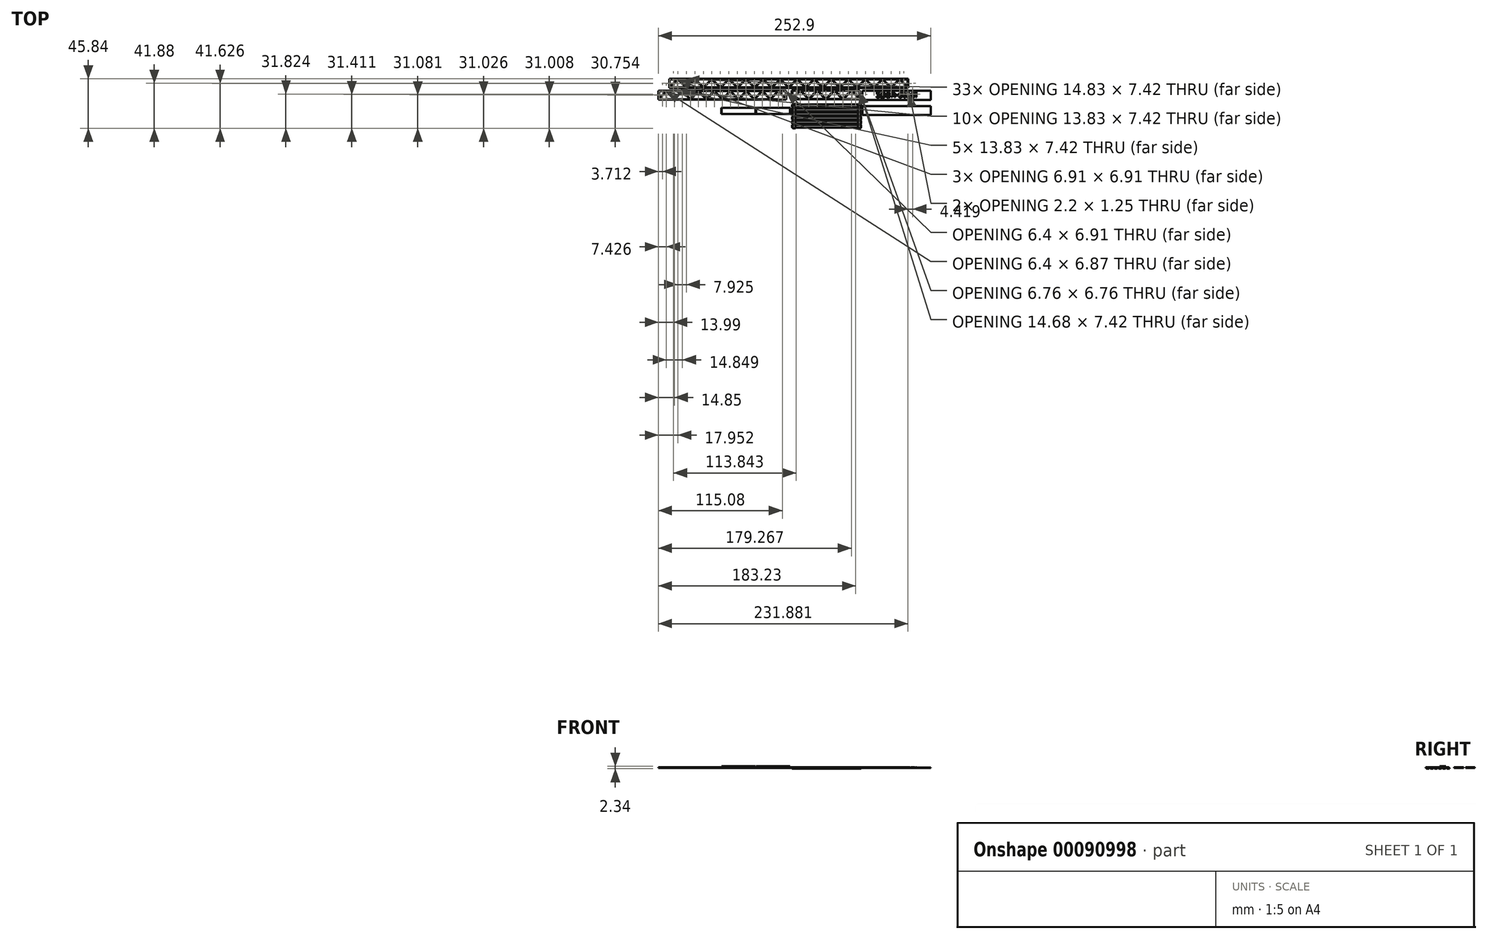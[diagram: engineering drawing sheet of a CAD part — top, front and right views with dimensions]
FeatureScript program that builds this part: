
annotation { "Feature Type Name" : "Feature", "Feature Type Description" : "" }
export const myFeature = defineFeature(function(context is Context, id is Id, definition is map)
    precondition{}
    {
        {
            var Q0;
            Q0=qCreatedBy(makeId("Top.planeOp"),FACE);
            var sketch = newSketch(context, id + "F0", { "sketchPlane" : qUnion([Q0])});
            skLineSegment(sketch, "E0.bottom", {"start": v(-2.9, 0) * mm, "end": v(-113.84, 0) * mm});
            skLineSegment(sketch, "E0.top", {"start": v(-2.9, 8.43) * mm, "end": v(-113.84, 8.43) * mm});
            skLineSegment(sketch, "E0.right", {"start": v(-113.84, 0) * mm, "end": v(-113.84, 8.43) * mm});
            skLineSegment(sketch, "E1.bottom", {"start": v(-113.33, 7.92) * mm, "end": v(-106.43, 7.92) * mm});
            skLineSegment(sketch, "E1.top", {"start": v(-113.33, 0.5) * mm, "end": v(-98.5, 0.5) * mm});
            skLineSegment(sketch, "E1.left", {"start": v(-113.33, 7.92) * mm, "end": v(-113.33, 1.02) * mm});
            skLineSegment(sketch, "E2", {"start": v(-113.33, 0.5) * mm, "end": v(-105.92, 7.92) * mm});
            skLineSegment(sketch, "E3", {"start": v(-113.33, 1.02) * mm, "end": v(-106.43, 7.92) * mm});
            skLineSegment(sketch, "E4.MirrorCS", {"start": v(-98.5, 0.5) * mm, "end": v(-105.92, 7.92) * mm});
            skLineSegment(sketch, "E5", {"start": v(-98, 0.5) * mm, "end": v(-105.41, 7.92) * mm});
            skLineSegment(sketch, "E6.MirrorCS", {"start": v(-98, 0.5) * mm, "end": v(-90.58, 7.92) * mm});
            skLineSegment(sketch, "E7.MirrorCS", {"start": v(-97.49, 0.5) * mm, "end": v(-90.07, 7.92) * mm});
            skLineSegment(sketch, "E8.MirrorCS", {"start": v(-82.65, 0.5) * mm, "end": v(-90.07, 7.92) * mm});
            skLineSegment(sketch, "E9.MirrorCS", {"start": v(-82.14, 0.5) * mm, "end": v(-89.56, 7.92) * mm});
            skLineSegment(sketch, "E10.MirrorCS", {"start": v(-82.14, 0.5) * mm, "end": v(-74.73, 7.92) * mm});
            skLineSegment(sketch, "E11.MirrorCS", {"start": v(-81.64, 0.5) * mm, "end": v(-74.22, 7.92) * mm});
            skLineSegment(sketch, "E12.MirrorCS", {"start": v(-66.8, 0.5) * mm, "end": v(-74.22, 7.92) * mm});
            skLineSegment(sketch, "E13.MirrorCS", {"start": v(-66.3, 0.5) * mm, "end": v(-73.71, 7.92) * mm});
            skLineSegment(sketch, "E14.MirrorCS", {"start": v(-66.3, 0.5) * mm, "end": v(-58.88, 7.92) * mm});
            skLineSegment(sketch, "E15.MirrorCS", {"start": v(-65.79, 0.5) * mm, "end": v(-58.37, 7.92) * mm});
            skLineSegment(sketch, "E16.MirrorCS", {"start": v(-50.95, 0.5) * mm, "end": v(-58.37, 7.92) * mm});
            skLineSegment(sketch, "E17.MirrorCS", {"start": v(-50.44, 0.5) * mm, "end": v(-57.86, 7.92) * mm});
            skLineSegment(sketch, "E18.MirrorCS", {"start": v(-50.44, 0.5) * mm, "end": v(-43.03, 7.92) * mm});
            skLineSegment(sketch, "E19.MirrorCS", {"start": v(-49.94, 0.5) * mm, "end": v(-42.52, 7.92) * mm});
            skLineSegment(sketch, "E20.MirrorCS", {"start": v(-35.1, 0.5) * mm, "end": v(-42.52, 7.92) * mm});
            skLineSegment(sketch, "E21.MirrorCS", {"start": v(-34.6, 0.5) * mm, "end": v(-42.01, 7.92) * mm});
            skLineSegment(sketch, "E22.MirrorCS", {"start": v(-34.6, 0.5) * mm, "end": v(-27.18, 7.92) * mm});
            skLineSegment(sketch, "E23.MirrorCS", {"start": v(-34.09, 0.5) * mm, "end": v(-26.67, 7.92) * mm});
            skLineSegment(sketch, "E24.MirrorCS", {"start": v(-19.25, 0.5) * mm, "end": v(-26.67, 7.92) * mm});
            skLineSegment(sketch, "E25.MirrorCS", {"start": v(-18.75, 0.5) * mm, "end": v(-26.16, 7.92) * mm});
            skLineSegment(sketch, "E26.MirrorCS", {"start": v(-18.75, 0.5) * mm, "end": v(-11.33, 7.92) * mm});
            skLineSegment(sketch, "E27.MirrorCS", {"start": v(-18.24, 0.5) * mm, "end": v(-10.82, 7.92) * mm});
            skLineSegment(sketch, "E28.MirrorCS", {"start": v(-2.9, 0.5) * mm, "end": v(-10.31, 7.92) * mm});
            skLineSegment(sketch, "E29.MirrorCS", {"start": v(-3.4, 0.5) * mm, "end": v(-10.82, 7.92) * mm});
            skLineSegment(sketch, "E30", {"start": v(-2.9, 0.5) * mm, "end": v(-2.9, 7.92) * mm});
            skLineSegment(sketch, "E31", {"start": v(-2.9, 7.92) * mm, "end": v(-2.9, 8.43) * mm});
            skLineSegment(sketch, "E32", {"start": v(-2.9, 8.43) * mm, "end": v(-2.9, 7.92) * mm});
            skLineSegment(sketch, "E33.trimOffspring", {"start": v(-10.31, 7.92) * mm, "end": v(-2.9, 7.92) * mm});
            skLineSegment(sketch, "E34.trimOffspring", {"start": v(-18.24, 0.5) * mm, "end": v(-3.4, 0.5) * mm});
            skLineSegment(sketch, "E35.trimOffspring", {"start": v(-26.16, 7.92) * mm, "end": v(-11.33, 7.92) * mm});
            skLineSegment(sketch, "E36.trimOffspring", {"start": v(-34.09, 0.5) * mm, "end": v(-19.25, 0.5) * mm});
            skLineSegment(sketch, "E37.trimOffspring", {"start": v(-49.94, 0.5) * mm, "end": v(-35.1, 0.5) * mm});
            skLineSegment(sketch, "E38.trimOffspring", {"start": v(-42.01, 7.92) * mm, "end": v(-27.18, 7.92) * mm});
            skLineSegment(sketch, "E39.trimOffspring", {"start": v(-57.86, 7.92) * mm, "end": v(-43.03, 7.92) * mm});
            skLineSegment(sketch, "E40.trimOffspring", {"start": v(-65.79, 0.5) * mm, "end": v(-50.95, 0.5) * mm});
            skLineSegment(sketch, "E41.trimOffspring", {"start": v(-81.64, 0.5) * mm, "end": v(-66.8, 0.5) * mm});
            skLineSegment(sketch, "E42.trimOffspring", {"start": v(-97.49, 0.5) * mm, "end": v(-82.65, 0.5) * mm});
            skLineSegment(sketch, "E43.trimOffspring", {"start": v(-105.41, 7.92) * mm, "end": v(-90.58, 7.92) * mm});
            skLineSegment(sketch, "E44.trimOffspring", {"start": v(-89.56, 7.92) * mm, "end": v(-74.73, 7.92) * mm});
            skLineSegment(sketch, "E45.trimOffspring", {"start": v(-73.71, 7.92) * mm, "end": v(-58.88, 7.92) * mm});
            skLineSegment(sketch, "E46.MirrorCS", {"start": v(12.95, 0.5) * mm, "end": v(20.37, 7.92) * mm});
            skLineSegment(sketch, "E47.MirrorCS", {"start": v(36.22, 7.92) * mm, "end": v(21.39, 7.92) * mm});
            skLineSegment(sketch, "E48.MirrorCS", {"start": v(28.8, 0.5) * mm, "end": v(21.39, 7.92) * mm});
            skLineSegment(sketch, "E49.MirrorCS", {"start": v(12.45, 0.5) * mm, "end": v(-2.39, 0.5) * mm});
            skLineSegment(sketch, "E50.MirrorCS", {"start": v(28.3, 0.5) * mm, "end": v(20.88, 7.92) * mm});
            skLineSegment(sketch, "E51.MirrorCS", {"start": v(-2.9, 8.43) * mm, "end": v(108.05, 8.43) * mm});
            skLineSegment(sketch, "E52.MirrorCS", {"start": v(12.95, 0.5) * mm, "end": v(5.54, 7.92) * mm});
            skLineSegment(sketch, "E53.MirrorCS", {"start": v(44.15, 0.5) * mm, "end": v(29.31, 0.5) * mm});
            skLineSegment(sketch, "E54.MirrorCS", {"start": v(28.3, 0.5) * mm, "end": v(13.46, 0.5) * mm});
            skLineSegment(sketch, "E55.MirrorCS", {"start": v(4.52, 7.92) * mm, "end": v(-2.9, 7.92) * mm});
            skLineSegment(sketch, "E56.MirrorCS", {"start": v(28.8, 0.5) * mm, "end": v(36.22, 7.92) * mm});
            skLineSegment(sketch, "E57.MirrorCS", {"start": v(13.46, 0.5) * mm, "end": v(20.88, 7.92) * mm});
            skLineSegment(sketch, "E58.MirrorCS", {"start": v(12.45, 0.5) * mm, "end": v(5.03, 7.92) * mm});
            skLineSegment(sketch, "E59.MirrorCS", {"start": v(29.31, 0.5) * mm, "end": v(36.73, 7.92) * mm});
            skLineSegment(sketch, "E60.MirrorCS", {"start": v(-2.9, 0.5) * mm, "end": v(4.52, 7.92) * mm});
            skLineSegment(sketch, "E61.MirrorCS", {"start": v(20.37, 7.92) * mm, "end": v(5.54, 7.92) * mm});
            skLineSegment(sketch, "E62.MirrorCS", {"start": v(-2.39, 0.5) * mm, "end": v(5.03, 7.92) * mm});
            skLineSegment(sketch, "E63.MirrorCS", {"start": v(-2.9, 0) * mm, "end": v(108.05, 0) * mm});
            skLineSegment(sketch, "E64.MirrorCS", {"start": v(107.54, 0.5) * mm, "end": v(100.13, 7.92) * mm});
            skLineSegment(sketch, "E65.MirrorCS", {"start": v(83.77, 7.92) * mm, "end": v(68.94, 7.92) * mm});
            skLineSegment(sketch, "E66.MirrorCS", {"start": v(61.01, 0.5) * mm, "end": v(68.43, 7.92) * mm});
            skLineSegment(sketch, "E67.MirrorCS", {"start": v(44.15, 0.5) * mm, "end": v(36.73, 7.92) * mm});
            skLineSegment(sketch, "E68.MirrorCS", {"start": v(99.62, 7.92) * mm, "end": v(84.79, 7.92) * mm});
            skLineSegment(sketch, "E69.MirrorCS", {"start": v(75.84, 0.5) * mm, "end": v(68.43, 7.92) * mm});
            skLineSegment(sketch, "E70.MirrorCS", {"start": v(44.65, 0.5) * mm, "end": v(37.24, 7.92) * mm});
            skLineSegment(sketch, "E71.MirrorCS", {"start": v(91.7, 0.5) * mm, "end": v(76.86, 0.5) * mm});
            skLineSegment(sketch, "E72.MirrorCS", {"start": v(76.35, 0.5) * mm, "end": v(68.94, 7.92) * mm});
            skLineSegment(sketch, "E73.MirrorCS", {"start": v(92.2, 0.5) * mm, "end": v(84.79, 7.92) * mm});
            skLineSegment(sketch, "E74.MirrorCS", {"start": v(108.05, 0) * mm, "end": v(108.05, 8.43) * mm});
            skLineSegment(sketch, "E75.MirrorCS", {"start": v(107.54, 7.92) * mm, "end": v(107.54, 1.02) * mm});
            skLineSegment(sketch, "E76.MirrorCS", {"start": v(107.54, 1.02) * mm, "end": v(100.63, 7.92) * mm});
            skLineSegment(sketch, "E77.MirrorCS", {"start": v(107.54, 7.92) * mm, "end": v(100.63, 7.92) * mm});
            skLineSegment(sketch, "E78.MirrorCS", {"start": v(76.35, 0.5) * mm, "end": v(83.77, 7.92) * mm});
            skLineSegment(sketch, "E79.MirrorCS", {"start": v(76.86, 0.5) * mm, "end": v(84.28, 7.92) * mm});
            skLineSegment(sketch, "E80.MirrorCS", {"start": v(107.54, 0.5) * mm, "end": v(92.7, 0.5) * mm});
            skLineSegment(sketch, "E81.MirrorCS", {"start": v(60.5, 0.5) * mm, "end": v(53.09, 7.92) * mm});
            skLineSegment(sketch, "E82.MirrorCS", {"start": v(52.07, 7.92) * mm, "end": v(37.24, 7.92) * mm});
            skLineSegment(sketch, "E83.MirrorCS", {"start": v(91.7, 0.5) * mm, "end": v(84.28, 7.92) * mm});
            skLineSegment(sketch, "E84.MirrorCS", {"start": v(67.92, 7.92) * mm, "end": v(53.09, 7.92) * mm});
            skLineSegment(sketch, "E85.MirrorCS", {"start": v(60, 0.5) * mm, "end": v(52.58, 7.92) * mm});
            skLineSegment(sketch, "E86.MirrorCS", {"start": v(75.84, 0.5) * mm, "end": v(61.01, 0.5) * mm});
            skLineSegment(sketch, "E87.MirrorCS", {"start": v(45.16, 0.5) * mm, "end": v(52.58, 7.92) * mm});
            skLineSegment(sketch, "E88.MirrorCS", {"start": v(60, 0.5) * mm, "end": v(45.16, 0.5) * mm});
            skLineSegment(sketch, "E89.MirrorCS", {"start": v(60.5, 0.5) * mm, "end": v(67.92, 7.92) * mm});
            skLineSegment(sketch, "E90.MirrorCS", {"start": v(44.65, 0.5) * mm, "end": v(52.07, 7.92) * mm});
            skLineSegment(sketch, "E91.MirrorCS", {"start": v(92.7, 0.5) * mm, "end": v(100.13, 7.92) * mm});
            skLineSegment(sketch, "E92.MirrorCS", {"start": v(92.2, 0.5) * mm, "end": v(99.62, 7.92) * mm});
            skPoint(sketch, "E93.MirrorCS.end.orphan", {"position": v(-2.9, 8.43) * mm});
            skPoint(sketch, "E94.MirrorCS.end.orphan", {"position": v(103.58, 4.47) * mm});
            skPoint(sketch, "E94.MirrorCS.start.orphan", {"position": v(104.09, 4.47) * mm});
            skPoint(sketch, "E95.MirrorCS.end.orphan", {"position": v(107.04, 1.02) * mm});
            skPoint(sketch, "E96.end.orphan", {"position": v(-109.37, 4.47) * mm});
            skPoint(sketch, "E96.start.orphan", {"position": v(-109.88, 4.47) * mm});
            skPoint(sketch, "E97.end.orphan", {"position": v(-112.83, 1.02) * mm});
            skSolve(sketch);
        }
        {
            var Q0;
            Q0 = qSketchRegion(id + "F0", true);
            extrude(context, id + "F1", {"entities" : qUnion([Q0]), "depth" : 0.5 * mm});
        }
        {
            var Q0;
            Q0=qCreatedBy(makeId("Top.planeOp"),FACE);
            var sketch = newSketch(context, id + "F2", { "sketchPlane" : qUnion([Q0])});
            skLineSegment(sketch, "E98.bottom", {"start": v(0, -2.11) * mm, "end": v(63.25, -2.11) * mm});
            skLineSegment(sketch, "E98.top", {"start": v(0, -10.55) * mm, "end": v(63.25, -10.55) * mm});
            skLineSegment(sketch, "E98.left", {"start": v(0, -2.11) * mm, "end": v(0, -10.55) * mm});
            skLineSegment(sketch, "E98.right", {"start": v(63.25, -2.11) * mm, "end": v(63.25, -10.55) * mm});
            skLineSegment(sketch, "E99.bottom", {"start": v(0.5, -2.62) * mm, "end": v(7.42, -2.62) * mm});
            skLineSegment(sketch, "E99.top", {"start": v(0.5, -10.04) * mm, "end": v(15.34, -10.04) * mm});
            skLineSegment(sketch, "E99.left", {"start": v(0.5, -2.62) * mm, "end": v(0.5, -9.53) * mm});
            skLineSegment(sketch, "E99.right", {"start": v(62.74, -2.62) * mm, "end": v(62.74, -9.38) * mm});
            skLineSegment(sketch, "E100", {"start": v(0.5, -10.04) * mm, "end": v(7.92, -2.62) * mm});
            skLineSegment(sketch, "E101", {"start": v(0.5, -9.53) * mm, "end": v(7.42, -2.62) * mm});
            skLineSegment(sketch, "E102.MirrorCS", {"start": v(15.34, -10.04) * mm, "end": v(7.92, -2.62) * mm});
            skLineSegment(sketch, "E103", {"start": v(15.85, -10.04) * mm, "end": v(8.43, -2.62) * mm});
            skLineSegment(sketch, "E104.trimOffspring", {"start": v(16.36, -10.04) * mm, "end": v(47.04, -10.04) * mm});
            skLineSegment(sketch, "E105.trimOffspring", {"start": v(8.43, -2.62) * mm, "end": v(23.27, -2.62) * mm});
            skLineSegment(sketch, "E106.MirrorCS", {"start": v(15.85, -10.04) * mm, "end": v(23.27, -2.62) * mm});
            skLineSegment(sketch, "E107.MirrorCS", {"start": v(16.36, -10.04) * mm, "end": v(23.77, -2.62) * mm});
            skLineSegment(sketch, "E108.trimOffspring", {"start": v(24.28, -2.62) * mm, "end": v(39.12, -2.62) * mm});
            skLineSegment(sketch, "E109.MirrorCS", {"start": v(31.2, -10.04) * mm, "end": v(23.77, -2.62) * mm});
            skLineSegment(sketch, "E110.MirrorCS", {"start": v(31.7, -10.04) * mm, "end": v(24.28, -2.62) * mm});
            skLineSegment(sketch, "E111.MirrorCS", {"start": v(31.7, -10.04) * mm, "end": v(39.12, -2.62) * mm});
            skLineSegment(sketch, "E112.MirrorCS", {"start": v(32.2, -10.04) * mm, "end": v(39.62, -2.62) * mm});
            skLineSegment(sketch, "E113.trimOffspring", {"start": v(40.13, -2.62) * mm, "end": v(54.97, -2.62) * mm});
            skLineSegment(sketch, "E114.MirrorCS", {"start": v(47.55, -10.04) * mm, "end": v(40.13, -2.62) * mm});
            skLineSegment(sketch, "E115.MirrorCS", {"start": v(47.04, -10.04) * mm, "end": v(39.62, -2.62) * mm});
            skLineSegment(sketch, "E116.MirrorCS", {"start": v(47.55, -10.04) * mm, "end": v(54.97, -2.62) * mm});
            skLineSegment(sketch, "E117.MirrorCS", {"start": v(48.06, -10.04) * mm, "end": v(55.47, -2.62) * mm});
            skLineSegment(sketch, "E118.trimOffspring", {"start": v(55.98, -2.62) * mm, "end": v(62.74, -2.62) * mm});
            skLineSegment(sketch, "E119.trimOffspring", {"start": v(62.74, -9.38) * mm, "end": v(55.98, -2.62) * mm});
            skLineSegment(sketch, "E120.trimOffspring", {"start": v(48.06, -10.04) * mm, "end": v(62.74, -10.04) * mm});
            skLineSegment(sketch, "E121", {"start": v(62.74, -10.04) * mm, "end": v(55.47, -2.62) * mm});
            skSolve(sketch);
        }
        {
            var Q0;
            Q0 = qSketchRegion(id + "F2", true);
            extrude(context, id + "F3", {"entities" : qUnion([Q0]), "depth" : 0.5 * mm});
        }
        {
            var Q0;
            Q0=qCreatedBy(makeId("Top.planeOp"),FACE);
            var sketch = newSketch(context, id + "F4", { "sketchPlane" : qUnion([Q0])});
            skLineSegment(sketch, "E122.bottom", {"start": v(-5.08, -2.44) * mm, "end": v(-123.36, -2.44) * mm});
            skLineSegment(sketch, "E122.top", {"start": v(-5.08, -10.87) * mm, "end": v(-123.36, -10.87) * mm});
            skLineSegment(sketch, "E122.left", {"start": v(-5.08, -2.44) * mm, "end": v(-5.08, -10.87) * mm});
            skLineSegment(sketch, "E123.bottom", {"start": v(-5.59, -2.95) * mm, "end": v(-12, -2.95) * mm});
            skLineSegment(sketch, "E123.top", {"start": v(-5.59, -10.36) * mm, "end": v(-19.42, -10.36) * mm});
            skLineSegment(sketch, "E123.left", {"start": v(-5.59, -2.95) * mm, "end": v(-5.59, -9.86) * mm});
            skLineSegment(sketch, "E124", {"start": v(-5.59, -10.36) * mm, "end": v(-12.5, -2.95) * mm});
            skLineSegment(sketch, "E125", {"start": v(-12, -2.95) * mm, "end": v(-5.59, -9.86) * mm});
            skLineSegment(sketch, "E126.MirrorCS", {"start": v(-19.42, -10.36) * mm, "end": v(-12.5, -2.95) * mm});
            skLineSegment(sketch, "E127.MirrorCS", {"start": v(-13.02, -2.95) * mm, "end": v(-19.37, -9.77) * mm});
            skLineSegment(sketch, "E128.trimOffspring", {"start": v(-13.02, -2.95) * mm, "end": v(-26.84, -2.95) * mm});
            skLineSegment(sketch, "E129", {"start": v(-19.37, -9.77) * mm, "end": v(-19.93, -10.36) * mm});
            skLineSegment(sketch, "E130.trimOffspring", {"start": v(-20.44, -10.36) * mm, "end": v(-34.27, -10.36) * mm});
            skLineSegment(sketch, "E131", {"start": v(-19.93, -10.36) * mm, "end": v(-13.02, -2.95) * mm});
            skLineSegment(sketch, "E132.MirrorCS", {"start": v(-19.93, -10.36) * mm, "end": v(-26.84, -2.95) * mm});
            skLineSegment(sketch, "E133.MirrorCS", {"start": v(-20.44, -10.36) * mm, "end": v(-27.35, -2.95) * mm});
            skLineSegment(sketch, "E134.trimOffspring", {"start": v(-27.86, -2.95) * mm, "end": v(-41.7, -2.95) * mm});
            skLineSegment(sketch, "E135.MirrorCS", {"start": v(-34.27, -10.36) * mm, "end": v(-27.35, -2.95) * mm});
            skLineSegment(sketch, "E136.MirrorCS", {"start": v(-34.78, -10.36) * mm, "end": v(-27.86, -2.95) * mm});
            skLineSegment(sketch, "E137.MirrorCS", {"start": v(-35.29, -10.36) * mm, "end": v(-42.2, -2.95) * mm});
            skLineSegment(sketch, "E138.MirrorCS", {"start": v(-41.7, -2.95) * mm, "end": v(-35.33, -9.77) * mm});
            skLineSegment(sketch, "E139.trimOffspring", {"start": v(-35.29, -10.36) * mm, "end": v(-49.12, -10.36) * mm});
            skLineSegment(sketch, "E140", {"start": v(-34.78, -10.36) * mm, "end": v(-35.33, -9.77) * mm});
            skLineSegment(sketch, "E141.trimOffspring", {"start": v(-42.71, -2.95) * mm, "end": v(-56.54, -2.95) * mm});
            skLineSegment(sketch, "E142.MirrorCS", {"start": v(-49.12, -10.36) * mm, "end": v(-42.2, -2.95) * mm});
            skLineSegment(sketch, "E143.MirrorCS", {"start": v(-42.71, -2.95) * mm, "end": v(-49.07, -9.77) * mm});
            skLineSegment(sketch, "E144.MirrorCS", {"start": v(-49.63, -10.36) * mm, "end": v(-49.07, -9.77) * mm});
            skLineSegment(sketch, "E145.MirrorCS", {"start": v(-49.63, -10.36) * mm, "end": v(-56.54, -2.95) * mm});
            skLineSegment(sketch, "E146.MirrorCS", {"start": v(-50.13, -10.36) * mm, "end": v(-57.05, -2.95) * mm});
            skLineSegment(sketch, "E147.MirrorCS", {"start": v(-64.47, -10.36) * mm, "end": v(-57.56, -2.95) * mm});
            skLineSegment(sketch, "E148.MirrorCS", {"start": v(-63.97, -10.36) * mm, "end": v(-57.05, -2.95) * mm});
            skLineSegment(sketch, "E149.MirrorCS", {"start": v(-71.39, -2.95) * mm, "end": v(-65.03, -9.77) * mm});
            skLineSegment(sketch, "E150.MirrorCS", {"start": v(-64.98, -10.36) * mm, "end": v(-71.9, -2.95) * mm});
            skLineSegment(sketch, "E151.MirrorCS", {"start": v(-64.47, -10.36) * mm, "end": v(-71.39, -2.95) * mm});
            skLineSegment(sketch, "E152.trimOffspring", {"start": v(-50.13, -10.36) * mm, "end": v(-63.97, -10.36) * mm});
            skLineSegment(sketch, "E153.trimOffspring", {"start": v(-64.98, -10.36) * mm, "end": v(-78.81, -10.36) * mm});
            skLineSegment(sketch, "E154.trimOffspring", {"start": v(-57.56, -2.95) * mm, "end": v(-71.39, -2.95) * mm});
            skLineSegment(sketch, "E155.trimOffspring", {"start": v(-72.4, -2.95) * mm, "end": v(-86.24, -2.95) * mm});
            skLineSegment(sketch, "E156.MirrorCS", {"start": v(-78.81, -10.36) * mm, "end": v(-71.9, -2.95) * mm});
            skLineSegment(sketch, "E157.MirrorCS", {"start": v(-72.4, -2.95) * mm, "end": v(-78.76, -9.77) * mm});
            skLineSegment(sketch, "E158.MirrorCS", {"start": v(-79.32, -10.36) * mm, "end": v(-86.24, -2.95) * mm});
            skLineSegment(sketch, "E159.MirrorCS", {"start": v(-79.83, -10.36) * mm, "end": v(-86.75, -2.95) * mm});
            skLineSegment(sketch, "E160.MirrorCS", {"start": v(-79.32, -10.36) * mm, "end": v(-72.4, -2.95) * mm});
            skLineSegment(sketch, "E161.MirrorCS", {"start": v(-93.66, -10.36) * mm, "end": v(-86.75, -2.95) * mm});
            skLineSegment(sketch, "E162.MirrorCS", {"start": v(-94.17, -10.36) * mm, "end": v(-87.26, -2.95) * mm});
            skLineSegment(sketch, "E163.MirrorCS", {"start": v(-94.17, -10.36) * mm, "end": v(-94.73, -9.77) * mm});
            skLineSegment(sketch, "E164.MirrorCS", {"start": v(-94.68, -10.36) * mm, "end": v(-101.6, -2.95) * mm});
            skLineSegment(sketch, "E165.MirrorCS", {"start": v(-108.51, -10.36) * mm, "end": v(-101.6, -2.95) * mm});
            skLineSegment(sketch, "E166.MirrorCS", {"start": v(-109.02, -10.36) * mm, "end": v(-108.46, -9.77) * mm});
            skLineSegment(sketch, "E167.MirrorCS", {"start": v(-102.1, -2.95) * mm, "end": v(-108.46, -9.77) * mm});
            skLineSegment(sketch, "E168.MirrorCS", {"start": v(-109.02, -10.36) * mm, "end": v(-115.93, -2.95) * mm});
            skLineSegment(sketch, "E169.MirrorCS", {"start": v(-109.53, -10.36) * mm, "end": v(-116.44, -2.95) * mm});
            skLineSegment(sketch, "E170.MirrorCS", {"start": v(-123.36, -10.36) * mm, "end": v(-116.44, -2.95) * mm});
            skLineSegment(sketch, "E171.MirrorCS", {"start": v(-123.36, -9.82) * mm, "end": v(-116.96, -2.95) * mm});
            skLineSegment(sketch, "E172.MirrorCS", {"start": v(-101.08, -2.95) * mm, "end": v(-94.73, -9.77) * mm});
            skLineSegment(sketch, "E173.trimOffspring", {"start": v(-79.83, -10.36) * mm, "end": v(-93.66, -10.36) * mm});
            skLineSegment(sketch, "E174.trimOffspring", {"start": v(-87.26, -2.95) * mm, "end": v(-101.08, -2.95) * mm});
            skLineSegment(sketch, "E175.trimOffspring", {"start": v(-94.68, -10.36) * mm, "end": v(-108.51, -10.36) * mm});
            skLineSegment(sketch, "E176.trimOffspring", {"start": v(-109.53, -10.36) * mm, "end": v(-123.36, -10.36) * mm});
            skLineSegment(sketch, "E177.trimOffspring", {"start": v(-102.1, -2.95) * mm, "end": v(-115.93, -2.95) * mm});
            skLineSegment(sketch, "E178.trimOffspring", {"start": v(-116.96, -2.95) * mm, "end": v(-123.36, -2.95) * mm});
            skLineSegment(sketch, "E179", {"start": v(-123.36, -9.82) * mm, "end": v(-123.36, -2.95) * mm});
            skLineSegment(sketch, "E180", {"start": v(-123.36, -2.95) * mm, "end": v(-123.36, -9.82) * mm});
            skLineSegment(sketch, "E181", {"start": v(-123.36, -10.87) * mm, "end": v(-123.87, -10.87) * mm});
            skLineSegment(sketch, "E182", {"start": v(-123.87, -10.87) * mm, "end": v(-123.87, -2.44) * mm});
            skLineSegment(sketch, "E183", {"start": v(-123.87, -2.44) * mm, "end": v(-123.36, -2.44) * mm});
            skSolve(sketch);
        }
        {
            var Q0;
            Q0 = qSketchRegion(id + "F4", true);
            extrude(context, id + "F5", {"entities" : qUnion([Q0]), "depth" : 0.5 * mm});
        }
        {
            var Q0;
            Q0=qCreatedBy(makeId("Top.planeOp"),FACE);
            var sketch = newSketch(context, id + "F6", { "sketchPlane" : qUnion([Q0])});
            skLineSegment(sketch, "E184.bottom", {"start": v(65.79, -2.54) * mm, "end": v(129.03, -2.54) * mm});
            skLineSegment(sketch, "E184.top", {"start": v(65.79, -10.97) * mm, "end": v(129.03, -10.97) * mm});
            skLineSegment(sketch, "E184.left", {"start": v(65.79, -2.54) * mm, "end": v(65.79, -10.97) * mm});
            skLineSegment(sketch, "E184.right", {"start": v(129.03, -2.54) * mm, "end": v(129.03, -10.97) * mm});
            skText(sketch, "E185", { "text": "Span-steel", "fontName": "OpenSans-Regular.ttf"});
            skLineSegment(sketch, "E186", {"start": v(83.43, -13.84) * mm, "end": v(94.5, -13.84) * mm});
            skLineSegment(sketch, "E187.MirrorCS", {"start": v(65.79, -16.7) * mm, "end": v(129.03, -16.7) * mm});
            skLineSegment(sketch, "E188.MirrorCS", {"start": v(65.79, -25.13) * mm, "end": v(65.79, -16.7) * mm});
            skLineSegment(sketch, "E189.MirrorCS", {"start": v(65.79, -25.13) * mm, "end": v(129.03, -25.13) * mm});
            skLineSegment(sketch, "E190.MirrorCS", {"start": v(129.03, -25.13) * mm, "end": v(129.03, -16.7) * mm});
            const initialGuessF6  = {"E185": [0.07836, -0.00872, 1, 0, 0.00567]};
            skSetInitialGuess(sketch, initialGuessF6);
            skSolve(sketch);
        }
        {
            var Q0;
            Q0 = qSketchRegion(id + "F6", true);
            var Q1;
            Q1=makeQuery(id+"F6.imprint","IMPRINT",FACE,{"disambiguationData":[TD([[makeQuery(id+"F6.imprint","IMPRINT",EDGE,{"derivedFrom":sQuery(id+"F6.wireOp",EDGE,"E185.sketch_text.stroke-50")}),-1.0]])]});
            var Q2;
            Q2=makeQuery(id+"F6.imprint","IMPRINT",FACE,{"disambiguationData":[TD([[makeQuery(id+"F6.imprint","IMPRINT",EDGE,{"derivedFrom":sQuery(id+"F6.wireOp",EDGE,"E185.sketch_text.stroke-0")}),-1.0]])]});
            var Q3;
            Q3=makeQuery(id+"F6.imprint","IMPRINT",FACE,{"disambiguationData":[TD([[makeQuery(id+"F6.imprint","IMPRINT",EDGE,{"derivedFrom":sQuery(id+"F6.wireOp",EDGE,"E185.sketch_text.stroke-41")}),1.0]])]});
            var Q4;
            Q4=makeQuery(id+"F6.imprint","IMPRINT",FACE,{"disambiguationData":[TD([[makeQuery(id+"F6.imprint","IMPRINT",EDGE,{"derivedFrom":sQuery(id+"F6.wireOp",EDGE,"E185.sketch_text.stroke-94")}),-1.0]])]});
            var Q5;
            Q5=makeQuery(id+"F6.imprint","IMPRINT",FACE,{"disambiguationData":[TD([[makeQuery(id+"F6.imprint","IMPRINT",EDGE,{"derivedFrom":sQuery(id+"F6.wireOp",EDGE,"E185.sketch_text.stroke-123")}),-1.0]])]});
            var Q6;
            Q6=makeQuery(id+"F6.imprint","IMPRINT",FACE,{"disambiguationData":[TD([[makeQuery(id+"F6.imprint","IMPRINT",EDGE,{"derivedFrom":sQuery(id+"F6.wireOp",EDGE,"E185.sketch_text.stroke-156")}),1.0]])]});
            var Q7;
            Q7=makeQuery(id+"F6.imprint","IMPRINT",FACE,{"disambiguationData":[TD([[makeQuery(id+"F6.imprint","IMPRINT",EDGE,{"derivedFrom":sQuery(id+"F6.wireOp",EDGE,"E185.sketch_text.stroke-180")}),-1.0]])]});
            var Q8;
            Q8=makeQuery(id+"F6.imprint","IMPRINT",FACE,{"disambiguationData":[TD([[makeQuery(id+"F6.imprint","IMPRINT",EDGE,{"derivedFrom":sQuery(id+"F6.wireOp",EDGE,"E185.sketch_text.stroke-25")}),-1.0]])]});
            var Q9;
            Q9=makeQuery(id+"F6.imprint","IMPRINT",FACE,{"disambiguationData":[TD([[makeQuery(id+"F6.imprint","IMPRINT",EDGE,{"derivedFrom":sQuery(id+"F6.wireOp",EDGE,"E185.sketch_text.stroke-142")}),-1.0]])]});
            var Q10;
            Q10=makeQuery(id+"F6.imprint","IMPRINT",FACE,{"disambiguationData":[TD([[makeQuery(id+"F6.imprint","IMPRINT",EDGE,{"derivedFrom":sQuery(id+"F6.wireOp",EDGE,"E185.sketch_text.stroke-161")}),-1.0]])]});
            var Q11;
            Q11=makeQuery(id+"F6.imprint","IMPRINT",FACE,{"disambiguationData":[TD([[makeQuery(id+"F6.imprint","IMPRINT",EDGE,{"derivedFrom":sQuery(id+"F6.wireOp",EDGE,"E184.bottom")}),-1.0]])]});
            var Q12;
            Q12=makeQuery(id+"F6.imprint","IMPRINT",FACE,{"disambiguationData":[TD([[makeQuery(id+"F6.imprint","IMPRINT",EDGE,{"derivedFrom":sQuery(id+"F6.wireOp",EDGE,"E185.sketch_text.stroke-77")}),-1.0]])]});
            var Q13;
            Q13=makeQuery(id+"F6.imprint","IMPRINT",FACE,{"disambiguationData":[TD([[makeQuery(id+"F6.imprint","IMPRINT",EDGE,{"derivedFrom":sQuery(id+"F6.wireOp",EDGE,"E185.sketch_text.stroke-98")}),-1.0]])]});
            var Q14;
            Q14=makeQuery(id+"F6.imprint","IMPRINT",FACE,{"disambiguationData":[TD([[makeQuery(id+"F6.imprint","IMPRINT",EDGE,{"derivedFrom":sQuery(id+"F6.wireOp",EDGE,"E185.sketch_text.stroke-69")}),1.0]])]});
            var Q15;
            Q15=makeQuery(id+"F6.imprint","IMPRINT",FACE,{"disambiguationData":[TD([[makeQuery(id+"F6.imprint","IMPRINT",EDGE,{"derivedFrom":sQuery(id+"F6.wireOp",EDGE,"E185.sketch_text.stroke-175")}),1.0]])]});
            extrude(context, id + "F7", {"entities" : qUnion([Q0, Q1, Q2, Q3, Q4, Q5, Q6, Q7, Q8, Q9, Q10, Q11, Q12, Q13, Q14, Q15]), "depth" : 0.25 * mm});
        }
        {
            var Q0;
            Q0=makeQuery(id+"F6.imprint","IMPRINT",FACE,{"disambiguationData":[TD([[makeQuery(id+"F6.imprint","IMPRINT",EDGE,{"derivedFrom":sQuery(id+"F6.wireOp",EDGE,"E185.sketch_text.stroke-0")}),-1.0]])]});
            var Q1;
            Q1=makeQuery(id+"F6.imprint","IMPRINT",FACE,{"disambiguationData":[TD([[makeQuery(id+"F6.imprint","IMPRINT",EDGE,{"derivedFrom":sQuery(id+"F6.wireOp",EDGE,"E185.sketch_text.stroke-25")}),-1.0]])]});
            var Q2;
            Q2=makeQuery(id+"F6.imprint","IMPRINT",FACE,{"disambiguationData":[TD([[makeQuery(id+"F6.imprint","IMPRINT",EDGE,{"derivedFrom":sQuery(id+"F6.wireOp",EDGE,"E185.sketch_text.stroke-50")}),-1.0]])]});
            var Q3;
            Q3=makeQuery(id+"F6.imprint","IMPRINT",FACE,{"disambiguationData":[TD([[makeQuery(id+"F6.imprint","IMPRINT",EDGE,{"derivedFrom":sQuery(id+"F6.wireOp",EDGE,"E185.sketch_text.stroke-77")}),-1.0]])]});
            var Q4;
            Q4=makeQuery(id+"F6.imprint","IMPRINT",FACE,{"disambiguationData":[TD([[makeQuery(id+"F6.imprint","IMPRINT",EDGE,{"derivedFrom":sQuery(id+"F6.wireOp",EDGE,"E185.sketch_text.stroke-94")}),-1.0]])]});
            var Q5;
            Q5=makeQuery(id+"F6.imprint","IMPRINT",FACE,{"disambiguationData":[TD([[makeQuery(id+"F6.imprint","IMPRINT",EDGE,{"derivedFrom":sQuery(id+"F6.wireOp",EDGE,"E185.sketch_text.stroke-98")}),-1.0]])]});
            var Q6;
            Q6=makeQuery(id+"F6.imprint","IMPRINT",FACE,{"disambiguationData":[TD([[makeQuery(id+"F6.imprint","IMPRINT",EDGE,{"derivedFrom":sQuery(id+"F6.wireOp",EDGE,"E185.sketch_text.stroke-123")}),-1.0]])]});
            var Q7;
            Q7=makeQuery(id+"F6.imprint","IMPRINT",FACE,{"disambiguationData":[TD([[makeQuery(id+"F6.imprint","IMPRINT",EDGE,{"derivedFrom":sQuery(id+"F6.wireOp",EDGE,"E185.sketch_text.stroke-161")}),-1.0]])]});
            var Q8;
            Q8=makeQuery(id+"F6.imprint","IMPRINT",FACE,{"disambiguationData":[TD([[makeQuery(id+"F6.imprint","IMPRINT",EDGE,{"derivedFrom":sQuery(id+"F6.wireOp",EDGE,"E185.sketch_text.stroke-142")}),-1.0]])]});
            var Q9;
            Q9=makeQuery(id+"F6.imprint","IMPRINT",FACE,{"disambiguationData":[TD([[makeQuery(id+"F6.imprint","IMPRINT",EDGE,{"derivedFrom":sQuery(id+"F6.wireOp",EDGE,"E185.sketch_text.stroke-180")}),-1.0]])]});
            extrude(context, id + "F8", {"entities" : qUnion([Q0, Q1, Q2, Q3, Q4, Q5, Q6, Q7, Q8, Q9]), "depth" : 0.5 * mm});
        }
        {
            var Q0;
            Q0=qCreatedBy(makeId("Top.planeOp"),FACE);
            var sketch = newSketch(context, id + "F9", { "sketchPlane" : qUnion([Q0])});
            skLineSegment(sketch, "E191.bottom", {"start": v(0.25, -15.19) * mm, "end": v(64.52, -15.19) * mm});
            skLineSegment(sketch, "E191.top", {"start": v(0.25, -17.73) * mm, "end": v(64.52, -17.73) * mm});
            skLineSegment(sketch, "E191.left", {"start": v(0.25, -15.19) * mm, "end": v(0.25, -17.73) * mm});
            skLineSegment(sketch, "E191.right", {"start": v(64.52, -15.19) * mm, "end": v(64.52, -17.73) * mm});
            skLineSegment(sketch, "E192.MirrorCS", {"start": v(0.25, -19) * mm, "end": v(64.52, -19) * mm});
            skLineSegment(sketch, "E193.MirrorCS", {"start": v(0.25, -21.54) * mm, "end": v(64.52, -21.54) * mm});
            skLineSegment(sketch, "E194", {"start": v(0.25, -19) * mm, "end": v(0.25, -21.54) * mm});
            skLineSegment(sketch, "E195", {"start": v(64.52, -19) * mm, "end": v(64.52, -21.54) * mm});
            skLineSegment(sketch, "E196.MirrorCS", {"start": v(0.25, -22.8) * mm, "end": v(64.52, -22.8) * mm});
            skLineSegment(sketch, "E197.MirrorCS", {"start": v(0.25, -25.35) * mm, "end": v(64.52, -25.35) * mm});
            skLineSegment(sketch, "E198.MirrorCS", {"start": v(0.25, -26.62) * mm, "end": v(64.52, -26.62) * mm});
            skLineSegment(sketch, "E199.MirrorCS", {"start": v(0.25, -29.16) * mm, "end": v(64.52, -29.16) * mm});
            skLineSegment(sketch, "E200.MirrorCS", {"start": v(64.52, -25.35) * mm, "end": v(64.52, -22.8) * mm});
            skLineSegment(sketch, "E201.MirrorCS", {"start": v(64.52, -29.16) * mm, "end": v(64.52, -26.62) * mm});
            skLineSegment(sketch, "E202.MirrorCS", {"start": v(0.25, -29.16) * mm, "end": v(0.25, -26.62) * mm});
            skLineSegment(sketch, "E203.MirrorCS", {"start": v(0.25, -25.35) * mm, "end": v(0.25, -22.8) * mm});
            skLineSegment(sketch, "E204.MirrorCS", {"start": v(0.25, -30.43) * mm, "end": v(64.52, -30.43) * mm});
            skLineSegment(sketch, "E205.MirrorCS", {"start": v(0.25, -32.97) * mm, "end": v(64.52, -32.97) * mm});
            skLineSegment(sketch, "E206.MirrorCS", {"start": v(0.25, -34.24) * mm, "end": v(64.52, -34.24) * mm});
            skLineSegment(sketch, "E207.MirrorCS", {"start": v(0.25, -36.78) * mm, "end": v(64.52, -36.78) * mm});
            skLineSegment(sketch, "E208.MirrorCS", {"start": v(64.52, -34.24) * mm, "end": v(64.52, -36.78) * mm});
            skLineSegment(sketch, "E209.MirrorCS", {"start": v(64.52, -30.43) * mm, "end": v(64.52, -32.97) * mm});
            skLineSegment(sketch, "E210.MirrorCS", {"start": v(0.25, -30.43) * mm, "end": v(0.25, -32.97) * mm});
            skLineSegment(sketch, "E211.MirrorCS", {"start": v(0.25, -34.24) * mm, "end": v(0.25, -36.78) * mm});
            skLineSegment(sketch, "E212.bottom", {"start": v(0.76, -15.82) * mm, "end": v(3.3, -15.82) * mm});
            skLineSegment(sketch, "E212.top", {"start": v(0.76, -37.41) * mm, "end": v(3.3, -37.41) * mm});
            skLineSegment(sketch, "E212.left", {"start": v(0.76, -15.82) * mm, "end": v(0.76, -37.41) * mm});
            skLineSegment(sketch, "E212.right", {"start": v(3.3, -15.82) * mm, "end": v(3.3, -37.41) * mm});
            skLineSegment(sketch, "E213.MirrorCS", {"start": v(61.47, -15.82) * mm, "end": v(61.47, -37.41) * mm});
            skLineSegment(sketch, "E214.MirrorCS", {"start": v(64, -15.82) * mm, "end": v(61.47, -15.82) * mm});
            skLineSegment(sketch, "E215.MirrorCS", {"start": v(64, -15.82) * mm, "end": v(64, -37.41) * mm});
            skLineSegment(sketch, "E216.MirrorCS", {"start": v(64, -37.41) * mm, "end": v(61.47, -37.41) * mm});
            skSolve(sketch);
        }
        {
            var Q0;
            Q0=makeQuery(id+"F9.imprint","IMPRINT",FACE,{"disambiguationData":[TD([[makeQuery(id+"F9.imprint","IMPRINT",EDGE,{"derivedFrom":sQuery(id+"F9.wireOp",EDGE,"E191.bottom")}),-1.0]])]});
            var Q1;
            {var subQ0=sQuery(id+"F9.wireOp",EDGE,"E212.right");var subQ1=sQuery(id+"F9.wireOp",EDGE,"E192.MirrorCS");var subQ2=makeQuery(id+"F9.imprint","INTERSECT",VERTEX,{"derivedFrom":[subQ1,subQ0]});Q1=makeQuery(id+"F9.imprint","IMPRINT",FACE,{"disambiguationData":[TD([[makeQuery(id+"F9.imprint","IMPRINT",EDGE,{"disambiguationData":[TD([[subQ2,-1.0]])],"derivedFrom":subQ1}),-1.0]])]});}
            var Q2;
            {var subQ0=sQuery(id+"F9.wireOp",EDGE,"E212.right");var subQ1=sQuery(id+"F9.wireOp",EDGE,"E196.MirrorCS");var subQ2=makeQuery(id+"F9.imprint","INTERSECT",VERTEX,{"derivedFrom":[subQ1,subQ0]});Q2=makeQuery(id+"F9.imprint","IMPRINT",FACE,{"disambiguationData":[TD([[makeQuery(id+"F9.imprint","IMPRINT",EDGE,{"disambiguationData":[TD([[subQ2,-1.0]])],"derivedFrom":subQ1}),-1.0]])]});}
            var Q3;
            {var subQ0=sQuery(id+"F9.wireOp",EDGE,"E212.right");var subQ1=sQuery(id+"F9.wireOp",EDGE,"E198.MirrorCS");var subQ2=makeQuery(id+"F9.imprint","INTERSECT",VERTEX,{"derivedFrom":[subQ1,subQ0]});Q3=makeQuery(id+"F9.imprint","IMPRINT",FACE,{"disambiguationData":[TD([[makeQuery(id+"F9.imprint","IMPRINT",EDGE,{"disambiguationData":[TD([[subQ2,-1.0]])],"derivedFrom":subQ1}),-1.0]])]});}
            var Q4;
            {var subQ0=sQuery(id+"F9.wireOp",EDGE,"E212.right");var subQ1=sQuery(id+"F9.wireOp",EDGE,"E204.MirrorCS");var subQ2=makeQuery(id+"F9.imprint","INTERSECT",VERTEX,{"derivedFrom":[subQ1,subQ0]});Q4=makeQuery(id+"F9.imprint","IMPRINT",FACE,{"disambiguationData":[TD([[makeQuery(id+"F9.imprint","IMPRINT",EDGE,{"disambiguationData":[TD([[subQ2,-1.0]])],"derivedFrom":subQ1}),-1.0]])]});}
            var Q5;
            {var subQ0=sQuery(id+"F9.wireOp",EDGE,"E212.right");var subQ1=sQuery(id+"F9.wireOp",EDGE,"E206.MirrorCS");var subQ2=makeQuery(id+"F9.imprint","INTERSECT",VERTEX,{"derivedFrom":[subQ1,subQ0]});Q5=makeQuery(id+"F9.imprint","IMPRINT",FACE,{"disambiguationData":[TD([[makeQuery(id+"F9.imprint","IMPRINT",EDGE,{"disambiguationData":[TD([[subQ2,-1.0]])],"derivedFrom":subQ1}),-1.0]])]});}
            var Q6;
            {var subQ0=sQuery(id+"F9.wireOp",EDGE,"E212.left");var subQ1=sQuery(id+"F9.wireOp",EDGE,"E206.MirrorCS");var subQ2=makeQuery(id+"F9.imprint","INTERSECT",VERTEX,{"derivedFrom":[subQ1,subQ0]});Q6=makeQuery(id+"F9.imprint","IMPRINT",FACE,{"disambiguationData":[TD([[makeQuery(id+"F9.imprint","IMPRINT",EDGE,{"disambiguationData":[TD([[subQ2,-1.0]])],"derivedFrom":subQ1}),-1.0]])]});}
            var Q7;
            {var subQ0=sQuery(id+"F9.wireOp",EDGE,"E211.MirrorCS");Q7=makeQuery(id+"F9.imprint","IMPRINT",FACE,{"disambiguationData":[TD([[makeQuery(id+"F9.imprint","IMPRINT",EDGE,{"derivedFrom":subQ0}),1.0]])]});}
            var Q8;
            {var subQ0=sQuery(id+"F9.wireOp",EDGE,"E212.left");var subQ1=sQuery(id+"F9.wireOp",EDGE,"E204.MirrorCS");var subQ2=makeQuery(id+"F9.imprint","INTERSECT",VERTEX,{"derivedFrom":[subQ1,subQ0]});Q8=makeQuery(id+"F9.imprint","IMPRINT",FACE,{"disambiguationData":[TD([[makeQuery(id+"F9.imprint","IMPRINT",EDGE,{"disambiguationData":[TD([[subQ2,-1.0]])],"derivedFrom":subQ1}),-1.0]])]});}
            var Q9;
            {var subQ0=sQuery(id+"F9.wireOp",EDGE,"E210.MirrorCS");Q9=makeQuery(id+"F9.imprint","IMPRINT",FACE,{"disambiguationData":[TD([[makeQuery(id+"F9.imprint","IMPRINT",EDGE,{"derivedFrom":subQ0}),1.0]])]});}
            var Q10;
            {var subQ0=sQuery(id+"F9.wireOp",EDGE,"E212.left");var subQ1=sQuery(id+"F9.wireOp",EDGE,"E198.MirrorCS");var subQ2=makeQuery(id+"F9.imprint","INTERSECT",VERTEX,{"derivedFrom":[subQ1,subQ0]});Q10=makeQuery(id+"F9.imprint","IMPRINT",FACE,{"disambiguationData":[TD([[makeQuery(id+"F9.imprint","IMPRINT",EDGE,{"disambiguationData":[TD([[subQ2,-1.0]])],"derivedFrom":subQ1}),-1.0]])]});}
            var Q11;
            {var subQ0=sQuery(id+"F9.wireOp",EDGE,"E202.MirrorCS");Q11=makeQuery(id+"F9.imprint","IMPRINT",FACE,{"disambiguationData":[TD([[makeQuery(id+"F9.imprint","IMPRINT",EDGE,{"derivedFrom":subQ0}),-1.0]])]});}
            var Q12;
            {var subQ0=sQuery(id+"F9.wireOp",EDGE,"E212.left");var subQ1=sQuery(id+"F9.wireOp",EDGE,"E196.MirrorCS");var subQ2=makeQuery(id+"F9.imprint","INTERSECT",VERTEX,{"derivedFrom":[subQ1,subQ0]});Q12=makeQuery(id+"F9.imprint","IMPRINT",FACE,{"disambiguationData":[TD([[makeQuery(id+"F9.imprint","IMPRINT",EDGE,{"disambiguationData":[TD([[subQ2,-1.0]])],"derivedFrom":subQ1}),-1.0]])]});}
            var Q13;
            {var subQ0=sQuery(id+"F9.wireOp",EDGE,"E203.MirrorCS");Q13=makeQuery(id+"F9.imprint","IMPRINT",FACE,{"disambiguationData":[TD([[makeQuery(id+"F9.imprint","IMPRINT",EDGE,{"derivedFrom":subQ0}),-1.0]])]});}
            var Q14;
            {var subQ0=sQuery(id+"F9.wireOp",EDGE,"E212.left");var subQ1=sQuery(id+"F9.wireOp",EDGE,"E192.MirrorCS");var subQ2=makeQuery(id+"F9.imprint","INTERSECT",VERTEX,{"derivedFrom":[subQ1,subQ0]});Q14=makeQuery(id+"F9.imprint","IMPRINT",FACE,{"disambiguationData":[TD([[makeQuery(id+"F9.imprint","IMPRINT",EDGE,{"disambiguationData":[TD([[subQ2,-1.0]])],"derivedFrom":subQ1}),-1.0]])]});}
            var Q15;
            {var subQ0=sQuery(id+"F9.wireOp",EDGE,"E194");Q15=makeQuery(id+"F9.imprint","IMPRINT",FACE,{"disambiguationData":[TD([[makeQuery(id+"F9.imprint","IMPRINT",EDGE,{"derivedFrom":subQ0}),1.0]])]});}
            var Q16;
            {var subQ5=sQuery(id+"F9.wireOp",EDGE,"E212.bottom");Q16=makeQuery(id+"F9.imprint","IMPRINT",FACE,{"disambiguationData":[TD([[makeQuery(id+"F9.imprint","IMPRINT",EDGE,{"derivedFrom":subQ5}),-1.0]])]});}
            var Q17;
            {var subQ5=sQuery(id+"F9.wireOp",EDGE,"E214.MirrorCS");Q17=makeQuery(id+"F9.imprint","IMPRINT",FACE,{"disambiguationData":[TD([[makeQuery(id+"F9.imprint","IMPRINT",EDGE,{"derivedFrom":subQ5}),1.0]])]});}
            var Q18;
            {var subQ0=sQuery(id+"F9.wireOp",EDGE,"E215.MirrorCS");var subQ1=sQuery(id+"F9.wireOp",EDGE,"E192.MirrorCS");var subQ2=makeQuery(id+"F9.imprint","INTERSECT",VERTEX,{"derivedFrom":[subQ1,subQ0]});Q18=makeQuery(id+"F9.imprint","IMPRINT",FACE,{"disambiguationData":[TD([[makeQuery(id+"F9.imprint","IMPRINT",EDGE,{"disambiguationData":[TD([[subQ2,1.0]])],"derivedFrom":subQ1}),-1.0]])]});}
            var Q19;
            {var subQ0=sQuery(id+"F9.wireOp",EDGE,"E195");Q19=makeQuery(id+"F9.imprint","IMPRINT",FACE,{"disambiguationData":[TD([[makeQuery(id+"F9.imprint","IMPRINT",EDGE,{"derivedFrom":subQ0}),-1.0]])]});}
            var Q20;
            {var subQ0=sQuery(id+"F9.wireOp",EDGE,"E200.MirrorCS");Q20=makeQuery(id+"F9.imprint","IMPRINT",FACE,{"disambiguationData":[TD([[makeQuery(id+"F9.imprint","IMPRINT",EDGE,{"derivedFrom":subQ0}),1.0]])]});}
            var Q21;
            {var subQ0=sQuery(id+"F9.wireOp",EDGE,"E215.MirrorCS");var subQ1=sQuery(id+"F9.wireOp",EDGE,"E196.MirrorCS");var subQ2=makeQuery(id+"F9.imprint","INTERSECT",VERTEX,{"derivedFrom":[subQ1,subQ0]});Q21=makeQuery(id+"F9.imprint","IMPRINT",FACE,{"disambiguationData":[TD([[makeQuery(id+"F9.imprint","IMPRINT",EDGE,{"disambiguationData":[TD([[subQ2,1.0]])],"derivedFrom":subQ1}),-1.0]])]});}
            var Q22;
            {var subQ0=sQuery(id+"F9.wireOp",EDGE,"E215.MirrorCS");var subQ1=sQuery(id+"F9.wireOp",EDGE,"E198.MirrorCS");var subQ2=makeQuery(id+"F9.imprint","INTERSECT",VERTEX,{"derivedFrom":[subQ1,subQ0]});Q22=makeQuery(id+"F9.imprint","IMPRINT",FACE,{"disambiguationData":[TD([[makeQuery(id+"F9.imprint","IMPRINT",EDGE,{"disambiguationData":[TD([[subQ2,1.0]])],"derivedFrom":subQ1}),-1.0]])]});}
            var Q23;
            {var subQ0=sQuery(id+"F9.wireOp",EDGE,"E201.MirrorCS");Q23=makeQuery(id+"F9.imprint","IMPRINT",FACE,{"disambiguationData":[TD([[makeQuery(id+"F9.imprint","IMPRINT",EDGE,{"derivedFrom":subQ0}),1.0]])]});}
            var Q24;
            {var subQ0=sQuery(id+"F9.wireOp",EDGE,"E209.MirrorCS");Q24=makeQuery(id+"F9.imprint","IMPRINT",FACE,{"disambiguationData":[TD([[makeQuery(id+"F9.imprint","IMPRINT",EDGE,{"derivedFrom":subQ0}),-1.0]])]});}
            var Q25;
            {var subQ0=sQuery(id+"F9.wireOp",EDGE,"E215.MirrorCS");var subQ1=sQuery(id+"F9.wireOp",EDGE,"E204.MirrorCS");var subQ2=makeQuery(id+"F9.imprint","INTERSECT",VERTEX,{"derivedFrom":[subQ1,subQ0]});Q25=makeQuery(id+"F9.imprint","IMPRINT",FACE,{"disambiguationData":[TD([[makeQuery(id+"F9.imprint","IMPRINT",EDGE,{"disambiguationData":[TD([[subQ2,1.0]])],"derivedFrom":subQ1}),-1.0]])]});}
            var Q26;
            {var subQ0=sQuery(id+"F9.wireOp",EDGE,"E215.MirrorCS");var subQ1=sQuery(id+"F9.wireOp",EDGE,"E206.MirrorCS");var subQ2=makeQuery(id+"F9.imprint","INTERSECT",VERTEX,{"derivedFrom":[subQ1,subQ0]});Q26=makeQuery(id+"F9.imprint","IMPRINT",FACE,{"disambiguationData":[TD([[makeQuery(id+"F9.imprint","IMPRINT",EDGE,{"disambiguationData":[TD([[subQ2,1.0]])],"derivedFrom":subQ1}),-1.0]])]});}
            var Q27;
            {var subQ0=sQuery(id+"F9.wireOp",EDGE,"E208.MirrorCS");Q27=makeQuery(id+"F9.imprint","IMPRINT",FACE,{"disambiguationData":[TD([[makeQuery(id+"F9.imprint","IMPRINT",EDGE,{"derivedFrom":subQ0}),-1.0]])]});}
            extrude(context, id + "F10", {"entities" : qUnion([Q0, Q1, Q2, Q3, Q4, Q5, Q6, Q7, Q8, Q9, Q10, Q11, Q12, Q13, Q14, Q15, Q16, Q17, Q18, Q19, Q20, Q21, Q22, Q23, Q24, Q25, Q26, Q27]), "oppositeDirection" : true, "depth" : 0.76 * mm});
        }
        {
            var Q0;
            {var subQ5=sQuery(id+"F9.wireOp",EDGE,"E212.bottom");Q0=makeQuery(id+"F9.imprint","IMPRINT",FACE,{"disambiguationData":[TD([[makeQuery(id+"F9.imprint","IMPRINT",EDGE,{"derivedFrom":subQ5}),-1.0]])]});}
            var Q1;
            {var subQ0=sQuery(id+"F9.wireOp",EDGE,"E212.left");var subQ1=sQuery(id+"F9.wireOp",EDGE,"E191.top");var subQ2=makeQuery(id+"F9.imprint","INTERSECT",VERTEX,{"derivedFrom":[subQ1,subQ0]});Q1=makeQuery(id+"F9.imprint","IMPRINT",FACE,{"disambiguationData":[TD([[makeQuery(id+"F9.imprint","IMPRINT",EDGE,{"disambiguationData":[TD([[subQ2,-1.0]])],"derivedFrom":subQ1}),-1.0]])]});}
            var Q2;
            {var subQ0=sQuery(id+"F9.wireOp",EDGE,"E212.left");var subQ1=sQuery(id+"F9.wireOp",EDGE,"E192.MirrorCS");var subQ2=makeQuery(id+"F9.imprint","INTERSECT",VERTEX,{"derivedFrom":[subQ1,subQ0]});Q2=makeQuery(id+"F9.imprint","IMPRINT",FACE,{"disambiguationData":[TD([[makeQuery(id+"F9.imprint","IMPRINT",EDGE,{"disambiguationData":[TD([[subQ2,-1.0]])],"derivedFrom":subQ1}),-1.0]])]});}
            var Q3;
            {var subQ0=sQuery(id+"F9.wireOp",EDGE,"E212.left");var subQ1=sQuery(id+"F9.wireOp",EDGE,"E193.MirrorCS");var subQ2=makeQuery(id+"F9.imprint","INTERSECT",VERTEX,{"derivedFrom":[subQ1,subQ0]});Q3=makeQuery(id+"F9.imprint","IMPRINT",FACE,{"disambiguationData":[TD([[makeQuery(id+"F9.imprint","IMPRINT",EDGE,{"disambiguationData":[TD([[subQ2,-1.0]])],"derivedFrom":subQ1}),-1.0]])]});}
            var Q4;
            {var subQ0=sQuery(id+"F9.wireOp",EDGE,"E212.left");var subQ1=sQuery(id+"F9.wireOp",EDGE,"E196.MirrorCS");var subQ2=makeQuery(id+"F9.imprint","INTERSECT",VERTEX,{"derivedFrom":[subQ1,subQ0]});Q4=makeQuery(id+"F9.imprint","IMPRINT",FACE,{"disambiguationData":[TD([[makeQuery(id+"F9.imprint","IMPRINT",EDGE,{"disambiguationData":[TD([[subQ2,-1.0]])],"derivedFrom":subQ1}),-1.0]])]});}
            var Q5;
            {var subQ0=sQuery(id+"F9.wireOp",EDGE,"E212.left");var subQ1=sQuery(id+"F9.wireOp",EDGE,"E197.MirrorCS");var subQ2=makeQuery(id+"F9.imprint","INTERSECT",VERTEX,{"derivedFrom":[subQ1,subQ0]});Q5=makeQuery(id+"F9.imprint","IMPRINT",FACE,{"disambiguationData":[TD([[makeQuery(id+"F9.imprint","IMPRINT",EDGE,{"disambiguationData":[TD([[subQ2,-1.0]])],"derivedFrom":subQ1}),-1.0]])]});}
            var Q6;
            {var subQ0=sQuery(id+"F9.wireOp",EDGE,"E212.left");var subQ1=sQuery(id+"F9.wireOp",EDGE,"E198.MirrorCS");var subQ2=makeQuery(id+"F9.imprint","INTERSECT",VERTEX,{"derivedFrom":[subQ1,subQ0]});Q6=makeQuery(id+"F9.imprint","IMPRINT",FACE,{"disambiguationData":[TD([[makeQuery(id+"F9.imprint","IMPRINT",EDGE,{"disambiguationData":[TD([[subQ2,-1.0]])],"derivedFrom":subQ1}),-1.0]])]});}
            var Q7;
            {var subQ0=sQuery(id+"F9.wireOp",EDGE,"E212.left");var subQ1=sQuery(id+"F9.wireOp",EDGE,"E199.MirrorCS");var subQ2=makeQuery(id+"F9.imprint","INTERSECT",VERTEX,{"derivedFrom":[subQ1,subQ0]});Q7=makeQuery(id+"F9.imprint","IMPRINT",FACE,{"disambiguationData":[TD([[makeQuery(id+"F9.imprint","IMPRINT",EDGE,{"disambiguationData":[TD([[subQ2,-1.0]])],"derivedFrom":subQ1}),-1.0]])]});}
            var Q8;
            {var subQ0=sQuery(id+"F9.wireOp",EDGE,"E212.left");var subQ1=sQuery(id+"F9.wireOp",EDGE,"E204.MirrorCS");var subQ2=makeQuery(id+"F9.imprint","INTERSECT",VERTEX,{"derivedFrom":[subQ1,subQ0]});Q8=makeQuery(id+"F9.imprint","IMPRINT",FACE,{"disambiguationData":[TD([[makeQuery(id+"F9.imprint","IMPRINT",EDGE,{"disambiguationData":[TD([[subQ2,-1.0]])],"derivedFrom":subQ1}),-1.0]])]});}
            var Q9;
            {var subQ0=sQuery(id+"F9.wireOp",EDGE,"E212.left");var subQ1=sQuery(id+"F9.wireOp",EDGE,"E205.MirrorCS");var subQ2=makeQuery(id+"F9.imprint","INTERSECT",VERTEX,{"derivedFrom":[subQ1,subQ0]});Q9=makeQuery(id+"F9.imprint","IMPRINT",FACE,{"disambiguationData":[TD([[makeQuery(id+"F9.imprint","IMPRINT",EDGE,{"disambiguationData":[TD([[subQ2,-1.0]])],"derivedFrom":subQ1}),-1.0]])]});}
            var Q10;
            {var subQ0=sQuery(id+"F9.wireOp",EDGE,"E212.left");var subQ1=sQuery(id+"F9.wireOp",EDGE,"E206.MirrorCS");var subQ2=makeQuery(id+"F9.imprint","INTERSECT",VERTEX,{"derivedFrom":[subQ1,subQ0]});Q10=makeQuery(id+"F9.imprint","IMPRINT",FACE,{"disambiguationData":[TD([[makeQuery(id+"F9.imprint","IMPRINT",EDGE,{"disambiguationData":[TD([[subQ2,-1.0]])],"derivedFrom":subQ1}),-1.0]])]});}
            var Q11;
            {var subQ5=sQuery(id+"F9.wireOp",EDGE,"E212.top");Q11=makeQuery(id+"F9.imprint","IMPRINT",FACE,{"disambiguationData":[TD([[makeQuery(id+"F9.imprint","IMPRINT",EDGE,{"derivedFrom":subQ5}),1.0]])]});}
            var Q12;
            {var subQ5=sQuery(id+"F9.wireOp",EDGE,"E214.MirrorCS");Q12=makeQuery(id+"F9.imprint","IMPRINT",FACE,{"disambiguationData":[TD([[makeQuery(id+"F9.imprint","IMPRINT",EDGE,{"derivedFrom":subQ5}),1.0]])]});}
            var Q13;
            {var subQ0=sQuery(id+"F9.wireOp",EDGE,"E215.MirrorCS");var subQ1=sQuery(id+"F9.wireOp",EDGE,"E191.top");var subQ2=makeQuery(id+"F9.imprint","INTERSECT",VERTEX,{"derivedFrom":[subQ1,subQ0]});Q13=makeQuery(id+"F9.imprint","IMPRINT",FACE,{"disambiguationData":[TD([[makeQuery(id+"F9.imprint","IMPRINT",EDGE,{"disambiguationData":[TD([[subQ2,1.0]])],"derivedFrom":subQ1}),-1.0]])]});}
            var Q14;
            {var subQ0=sQuery(id+"F9.wireOp",EDGE,"E215.MirrorCS");var subQ1=sQuery(id+"F9.wireOp",EDGE,"E192.MirrorCS");var subQ2=makeQuery(id+"F9.imprint","INTERSECT",VERTEX,{"derivedFrom":[subQ1,subQ0]});Q14=makeQuery(id+"F9.imprint","IMPRINT",FACE,{"disambiguationData":[TD([[makeQuery(id+"F9.imprint","IMPRINT",EDGE,{"disambiguationData":[TD([[subQ2,1.0]])],"derivedFrom":subQ1}),-1.0]])]});}
            var Q15;
            {var subQ0=sQuery(id+"F9.wireOp",EDGE,"E215.MirrorCS");var subQ1=sQuery(id+"F9.wireOp",EDGE,"E193.MirrorCS");var subQ2=makeQuery(id+"F9.imprint","INTERSECT",VERTEX,{"derivedFrom":[subQ1,subQ0]});Q15=makeQuery(id+"F9.imprint","IMPRINT",FACE,{"disambiguationData":[TD([[makeQuery(id+"F9.imprint","IMPRINT",EDGE,{"disambiguationData":[TD([[subQ2,1.0]])],"derivedFrom":subQ1}),-1.0]])]});}
            var Q16;
            {var subQ0=sQuery(id+"F9.wireOp",EDGE,"E215.MirrorCS");var subQ1=sQuery(id+"F9.wireOp",EDGE,"E196.MirrorCS");var subQ2=makeQuery(id+"F9.imprint","INTERSECT",VERTEX,{"derivedFrom":[subQ1,subQ0]});Q16=makeQuery(id+"F9.imprint","IMPRINT",FACE,{"disambiguationData":[TD([[makeQuery(id+"F9.imprint","IMPRINT",EDGE,{"disambiguationData":[TD([[subQ2,1.0]])],"derivedFrom":subQ1}),-1.0]])]});}
            var Q17;
            {var subQ0=sQuery(id+"F9.wireOp",EDGE,"E215.MirrorCS");var subQ1=sQuery(id+"F9.wireOp",EDGE,"E197.MirrorCS");var subQ2=makeQuery(id+"F9.imprint","INTERSECT",VERTEX,{"derivedFrom":[subQ1,subQ0]});Q17=makeQuery(id+"F9.imprint","IMPRINT",FACE,{"disambiguationData":[TD([[makeQuery(id+"F9.imprint","IMPRINT",EDGE,{"disambiguationData":[TD([[subQ2,1.0]])],"derivedFrom":subQ1}),-1.0]])]});}
            var Q18;
            {var subQ0=sQuery(id+"F9.wireOp",EDGE,"E215.MirrorCS");var subQ1=sQuery(id+"F9.wireOp",EDGE,"E198.MirrorCS");var subQ2=makeQuery(id+"F9.imprint","INTERSECT",VERTEX,{"derivedFrom":[subQ1,subQ0]});Q18=makeQuery(id+"F9.imprint","IMPRINT",FACE,{"disambiguationData":[TD([[makeQuery(id+"F9.imprint","IMPRINT",EDGE,{"disambiguationData":[TD([[subQ2,1.0]])],"derivedFrom":subQ1}),-1.0]])]});}
            var Q19;
            {var subQ0=sQuery(id+"F9.wireOp",EDGE,"E215.MirrorCS");var subQ1=sQuery(id+"F9.wireOp",EDGE,"E199.MirrorCS");var subQ2=makeQuery(id+"F9.imprint","INTERSECT",VERTEX,{"derivedFrom":[subQ1,subQ0]});Q19=makeQuery(id+"F9.imprint","IMPRINT",FACE,{"disambiguationData":[TD([[makeQuery(id+"F9.imprint","IMPRINT",EDGE,{"disambiguationData":[TD([[subQ2,1.0]])],"derivedFrom":subQ1}),-1.0]])]});}
            var Q20;
            {var subQ0=sQuery(id+"F9.wireOp",EDGE,"E215.MirrorCS");var subQ1=sQuery(id+"F9.wireOp",EDGE,"E204.MirrorCS");var subQ2=makeQuery(id+"F9.imprint","INTERSECT",VERTEX,{"derivedFrom":[subQ1,subQ0]});Q20=makeQuery(id+"F9.imprint","IMPRINT",FACE,{"disambiguationData":[TD([[makeQuery(id+"F9.imprint","IMPRINT",EDGE,{"disambiguationData":[TD([[subQ2,1.0]])],"derivedFrom":subQ1}),-1.0]])]});}
            var Q21;
            {var subQ0=sQuery(id+"F9.wireOp",EDGE,"E215.MirrorCS");var subQ1=sQuery(id+"F9.wireOp",EDGE,"E205.MirrorCS");var subQ2=makeQuery(id+"F9.imprint","INTERSECT",VERTEX,{"derivedFrom":[subQ1,subQ0]});Q21=makeQuery(id+"F9.imprint","IMPRINT",FACE,{"disambiguationData":[TD([[makeQuery(id+"F9.imprint","IMPRINT",EDGE,{"disambiguationData":[TD([[subQ2,1.0]])],"derivedFrom":subQ1}),-1.0]])]});}
            var Q22;
            {var subQ0=sQuery(id+"F9.wireOp",EDGE,"E215.MirrorCS");var subQ1=sQuery(id+"F9.wireOp",EDGE,"E206.MirrorCS");var subQ2=makeQuery(id+"F9.imprint","INTERSECT",VERTEX,{"derivedFrom":[subQ1,subQ0]});Q22=makeQuery(id+"F9.imprint","IMPRINT",FACE,{"disambiguationData":[TD([[makeQuery(id+"F9.imprint","IMPRINT",EDGE,{"disambiguationData":[TD([[subQ2,1.0]])],"derivedFrom":subQ1}),-1.0]])]});}
            var Q23;
            {var subQ5=sQuery(id+"F9.wireOp",EDGE,"E216.MirrorCS");Q23=makeQuery(id+"F9.imprint","IMPRINT",FACE,{"disambiguationData":[TD([[makeQuery(id+"F9.imprint","IMPRINT",EDGE,{"derivedFrom":subQ5}),-1.0]])]});}
            extrude(context, id + "F11", {"entities" : qUnion([Q0, Q1, Q2, Q3, Q4, Q5, Q6, Q7, Q8, Q9, Q10, Q11, Q12, Q13, Q14, Q15, Q16, Q17, Q18, Q19, Q20, Q21, Q22, Q23]), "depth" : 0.5 * mm});
        }
        {
            var Q0;
            Q0=qCreatedBy(makeId("Top.planeOp"),FACE);
            var sketch = newSketch(context, id + "F12", { "sketchPlane" : qUnion([Q0])});
            skLineSegment(sketch, "E217.bottom", {"start": v(-65.53, -18.55) * mm, "end": v(-1.27, -18.55) * mm});
            skLineSegment(sketch, "E217.top", {"start": v(-65.53, -24.13) * mm, "end": v(-1.27, -24.13) * mm});
            skLineSegment(sketch, "E217.left", {"start": v(-65.53, -18.55) * mm, "end": v(-65.53, -24.13) * mm});
            skLineSegment(sketch, "E217.right", {"start": v(-1.27, -18.55) * mm, "end": v(-1.27, -24.13) * mm});
            skLineSegment(sketch, "E218", {"start": v(-65.02, -18.55) * mm, "end": v(-65.02, -24.13) * mm});
            skLineSegment(sketch, "E219", {"start": v(-33.65, -18.55) * mm, "end": v(-33.65, -24.13) * mm});
            skLineSegment(sketch, "E220", {"start": v(-1.78, -18.55) * mm, "end": v(-1.78, -24.13) * mm});
            skLineSegment(sketch, "E221", {"start": v(-33.15, -18.55) * mm, "end": v(-33.15, -24.13) * mm});
            skPoint(sketch, "E222.end.orphan", {"position": v(-33.4, -24.13) * mm});
            skPoint(sketch, "E222.start.orphan", {"position": v(-33.4, -18.55) * mm});
            skSolve(sketch);
        }
        {
            var Q0;
            Q0=makeQuery(id+"F12.imprint","IMPRINT",FACE,{"disambiguationData":[TD([[makeQuery(id+"F12.imprint","IMPRINT",EDGE,{"derivedFrom":sQuery(id+"F12.wireOp",EDGE,"E217.bottom")}),-1.0]])]});
            extrude(context, id + "F13", {"entities" : qUnion([Q0]), "depth" : 0.25 * mm});
        }
        {
            var Q0;
            {var subQ0=sQuery(id+"F12.wireOp",EDGE,"E218");Q0=makeQuery(id+"F12.imprint","IMPRINT",FACE,{"disambiguationData":[TD([[makeQuery(id+"F12.imprint","IMPRINT",EDGE,{"derivedFrom":subQ0}),1.0]])]});}
            var Q1;
            {var subQ0=sQuery(id+"F12.wireOp",EDGE,"E220");Q1=makeQuery(id+"F12.imprint","IMPRINT",FACE,{"disambiguationData":[TD([[makeQuery(id+"F12.imprint","IMPRINT",EDGE,{"derivedFrom":subQ0}),-1.0]])]});}
            extrude(context, id + "F14", {"entities" : qUnion([Q0, Q1]), "depth" : 1.58 * mm});
        }
    });
